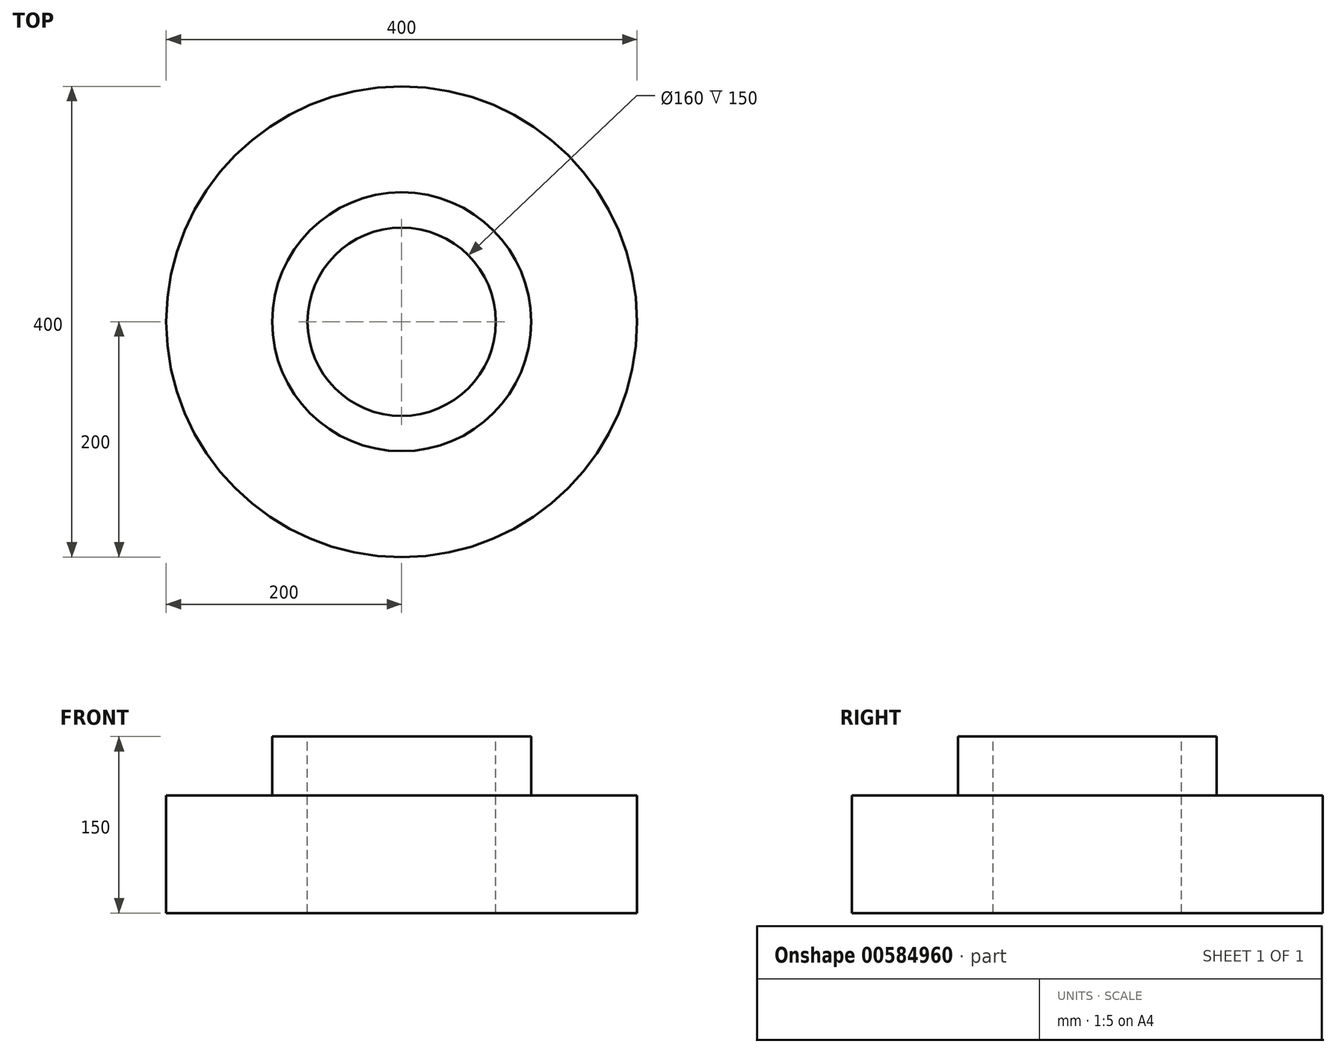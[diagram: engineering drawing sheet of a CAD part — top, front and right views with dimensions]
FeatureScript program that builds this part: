
annotation { "Feature Type Name" : "Feature", "Feature Type Description" : "" }
export const myFeature = defineFeature(function(context is Context, id is Id, definition is map)
    precondition{}
    {
        {
            var Q0;
            Q0=qCreatedBy(makeId("Front.planeOp"),FACE);
            var sketch = newSketch(context, id + "F0", { "sketchPlane" : qUnion([Q0])});
            skLineSegment(sketch, "E0", {"start": v(0, 0) * mm, "end": v(0, 150) * mm, "construction": true});
            skLineSegment(sketch, "E1", {"start": v(0, 0) * mm, "end": v(200, 0) * mm});
            skLineSegment(sketch, "E2", {"start": v(200, 0) * mm, "end": v(200, 100) * mm});
            skLineSegment(sketch, "E3", {"start": v(200, 100) * mm, "end": v(110, 100) * mm});
            skLineSegment(sketch, "E4", {"start": v(110, 100) * mm, "end": v(110, 150) * mm});
            skLineSegment(sketch, "E5", {"start": v(110, 150) * mm, "end": v(0, 150) * mm});
            skLineSegment(sketch, "E6", {"start": v(0, 150) * mm, "end": v(0, 0) * mm});
            skSolve(sketch);
        }
        {
            var Q0;
            Q0 = qSketchRegion(id + "F0", true);
            var Q1;
            Q1=sQuery(id+"F0.wireOp",EDGE,"E0");
            revolve(context, id + "F1", {"entities" : qUnion([Q0]), "axis" : qUnion([Q1]), "revolveType" : RevolveType.FULL});
        }
        {
            var Q0;
            Q0=makeQuery(id+"F1.opRevolve","SWEPT_FACE",FACE,{"disambiguationData":[OSD([sQuery(id+"F0.wireOp",EDGE,"E5")])]});
            var sketch = newSketch(context, id + "F2", { "sketchPlane" : qUnion([Q0])});
            skPoint(sketch, "E7", {"position": v(0, 0) * mm});
            skSolve(sketch);
        }
        {
            var Q0;
            Q0=sQuery(id+"F2.wireOp",VERTEX,"E7");
            var Q1;
            Q1=makeQuery(id+"F1.opRevolve","SWEPT_BODY",BODY,{"disambiguationData":[OSD([sQuery(id+"F0.wireOp",EDGE,"E1"),sQuery(id+"F0.wireOp",EDGE,"E2"),sQuery(id+"F0.wireOp",EDGE,"E3"),sQuery(id+"F0.wireOp",EDGE,"E4"),sQuery(id+"F0.wireOp",EDGE,"E5"),sQuery(id+"F0.wireOp",EDGE,"E6")])]});
            hole(context, id + "F3", {"style" : HoleStyle.SIMPLE, "endStyle" : HoleEndStyle.THROUGH, "holeDiameter" : 160 * mm, "majorDiameter" : 5 * mm, "isTappedThrough" : true, "tappedDepth" : 12 * mm, "tapClearance" : 3, "locations" : qUnion([Q0]), "scope" : qUnion([Q1])});
        }
    });
